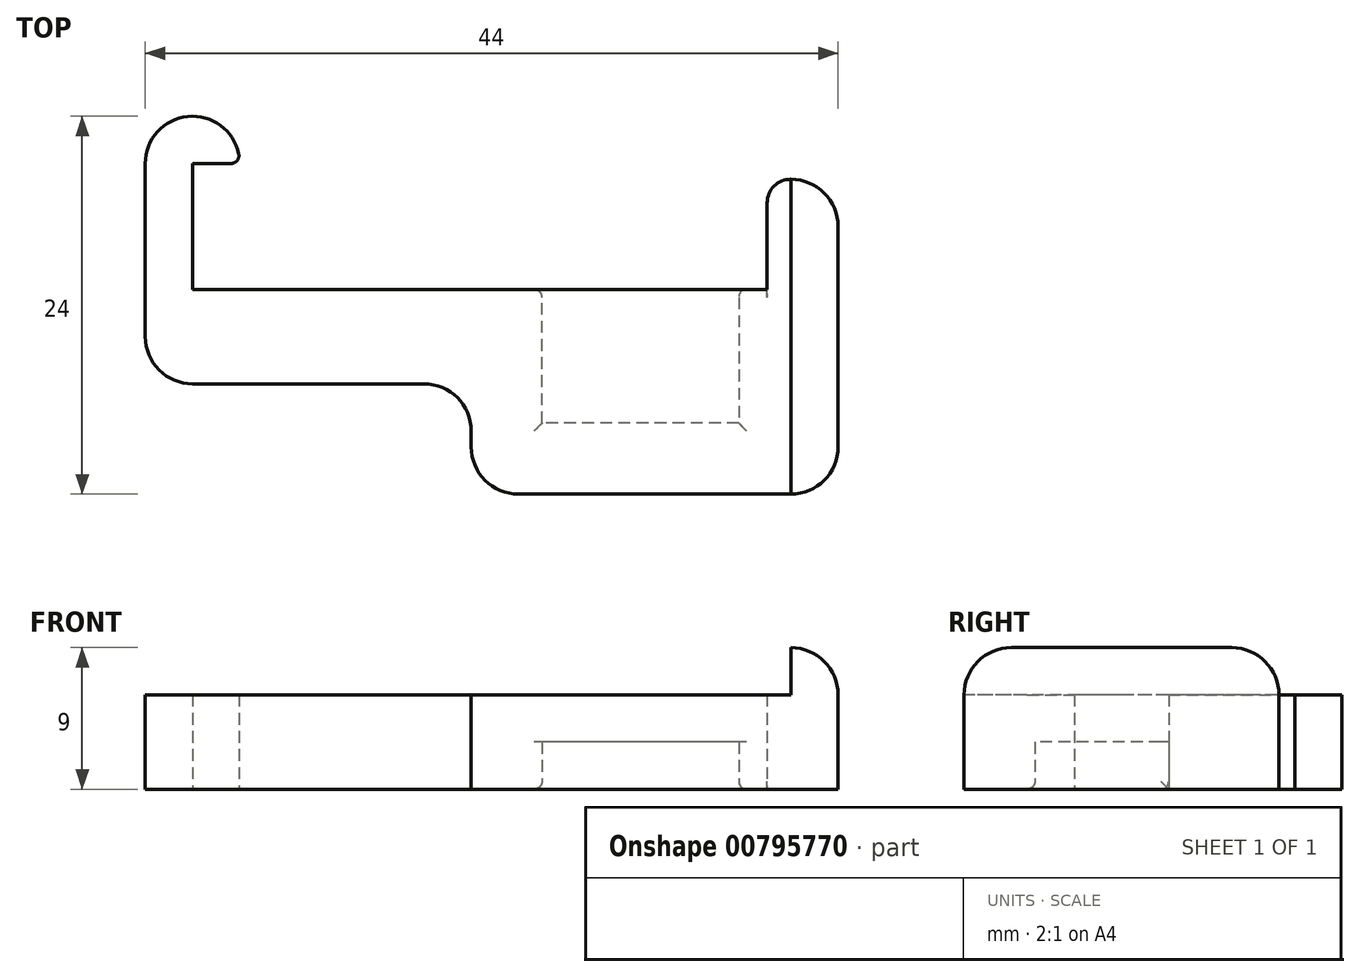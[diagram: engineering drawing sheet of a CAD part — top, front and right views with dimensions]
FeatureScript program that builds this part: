
annotation { "Feature Type Name" : "Feature", "Feature Type Description" : "" }
export const myFeature = defineFeature(function(context is Context, id is Id, definition is map)
    precondition{}
    {
        {
            var Q0;
            Q0=qCreatedBy(makeId("Top.planeOp"),FACE);
            var sketch = newSketch(context, id + "F0", { "sketchPlane" : qUnion([Q0])});
            skLineSegment(sketch, "E0", {"start": v(-39.5, -6) * mm, "end": v(-18.8, -6) * mm});
            skLineSegment(sketch, "E1", {"start": v(-18.8, -6) * mm, "end": v(-18.8, -13) * mm});
            skLineSegment(sketch, "E2", {"start": v(-18.8, -13) * mm, "end": v(4.5, -13) * mm});
            skLineSegment(sketch, "E3", {"start": v(4.5, -13) * mm, "end": v(4.5, 7) * mm});
            skLineSegment(sketch, "E4", {"start": v(4.5, 7) * mm, "end": v(0, 7) * mm});
            skLineSegment(sketch, "E5", {"start": v(0, 7) * mm, "end": v(0, 0) * mm});
            skLineSegment(sketch, "E6", {"start": v(0, 0) * mm, "end": v(-36.5, 0) * mm});
            skLineSegment(sketch, "E7", {"start": v(-36.5, 0) * mm, "end": v(-36.5, 8) * mm});
            skLineSegment(sketch, "E8", {"start": v(-36.5, 8) * mm, "end": v(-33.5, 8) * mm});
            skLineSegment(sketch, "E9", {"start": v(-33.5, 8) * mm, "end": v(-33.5, 11) * mm});
            skLineSegment(sketch, "E10", {"start": v(-33.5, 11) * mm, "end": v(-39.5, 11) * mm});
            skLineSegment(sketch, "E11", {"start": v(-39.5, 11) * mm, "end": v(-39.5, -6) * mm});
            skLineSegment(sketch, "E12", {"start": v(-1.8, 0) * mm, "end": v(-1.8, -8.5) * mm});
            skLineSegment(sketch, "E13", {"start": v(-1.8, -8.5) * mm, "end": v(-14.3, -8.5) * mm});
            skLineSegment(sketch, "E14", {"start": v(-14.3, -8.5) * mm, "end": v(-14.3, 0) * mm});
            skLineSegment(sketch, "E15", {"start": v(1.5, 7) * mm, "end": v(1.5, -13) * mm});
            skSolve(sketch);
        }
        {
            var Q0;
            Q0=makeQuery(id+"F0.imprint","IMPRINT",FACE,{"disambiguationData":[TD([[makeQuery(id+"F0.imprint","IMPRINT",EDGE,{"derivedFrom":sQuery(id+"F0.wireOp",EDGE,"E0")}),1.0]])]});
            extrude(context, id + "F1", {"entities" : qUnion([Q0]), "depth" : 1.5 * mm, "offsetDistance" : 25 * mm, "hasSecondDirection" : true, "secondDirectionOppositeDirection" : true, "secondDirectionDepth" : 4.5 * mm});
        }
        {
            var Q0;
            {var subQ0=sQuery(id+"F0.wireOp",EDGE,"E12");Q0=makeQuery(id+"F0.imprint","IMPRINT",FACE,{"disambiguationData":[TD([[makeQuery(id+"F0.imprint","IMPRINT",EDGE,{"derivedFrom":subQ0}),-1.0]])]});}
            extrude(context, id + "F2", {"entities" : qUnion([Q0]), "operationType" : NewBodyOperationType.ADD, "depth" : 1.5 * mm, "offsetDistance" : 25 * mm, "hasSecondDirection" : true, "secondDirectionOppositeDirection" : true, "secondDirectionDepth" : 1.5 * mm});
        }
        {
            var Q0;
            {var subQ0=sQuery(id+"F0.wireOp",EDGE,"E3");Q0=makeQuery(id+"F0.imprint","IMPRINT",FACE,{"disambiguationData":[TD([[makeQuery(id+"F0.imprint","IMPRINT",EDGE,{"derivedFrom":subQ0}),1.0]])]});}
            extrude(context, id + "F3", {"entities" : qUnion([Q0]), "operationType" : NewBodyOperationType.ADD, "depth" : 4.5 * mm, "offsetDistance" : 25 * mm, "hasSecondDirection" : true, "secondDirectionOppositeDirection" : true, "secondDirectionDepth" : 4.5 * mm});
        }
        {
            var Q0;
            Q0=makeQuery(id+"F1.opExtrude","SWEPT_EDGE",EDGE,{"disambiguationData":[OSD([sQuery(id+"F0.wireOp",EDGE,"E10"),sQuery(id+"F0.wireOp",EDGE,"E11")])]});
            var Q1;
            Q1=makeQuery(id+"F1.opExtrude","SWEPT_EDGE",EDGE,{"disambiguationData":[OSD([sQuery(id+"F0.wireOp",EDGE,"E9"),sQuery(id+"F0.wireOp",EDGE,"E10")])]});
            var Q2;
            Q2=makeQuery(id+"F1.opExtrude","SWEPT_EDGE",EDGE,{"disambiguationData":[OSD([sQuery(id+"F0.wireOp",EDGE,"E0"),sQuery(id+"F0.wireOp",EDGE,"E11")])]});
            var Q3;
            Q3=makeQuery(id+"F1.opExtrude","SWEPT_EDGE",EDGE,{"disambiguationData":[OSD([sQuery(id+"F0.wireOp",EDGE,"E0"),sQuery(id+"F0.wireOp",EDGE,"E1")])]});
            var Q4;
            Q4=makeQuery(id+"F1.opExtrude","SWEPT_EDGE",EDGE,{"disambiguationData":[OSD([sQuery(id+"F0.wireOp",EDGE,"E1"),sQuery(id+"F0.wireOp",EDGE,"E2")])]});
            var Q5;
            Q5=makeQuery(id+"F3.opExtrude","CAP_EDGE",EDGE,{"disambiguationData":[OSD([sQuery(id+"F0.wireOp",EDGE,"E4")])],"isStart":false});
            var Q6;
            Q6=makeQuery(id+"F3.opExtrude","SWEPT_EDGE",EDGE,{"disambiguationData":[OSD([sQuery(id+"F0.wireOp",EDGE,"E3"),sQuery(id+"F0.wireOp",EDGE,"E4")])]});
            var Q7;
            Q7=makeQuery(id+"F3.opExtrude","CAP_EDGE",EDGE,{"disambiguationData":[OSD([sQuery(id+"F0.wireOp",EDGE,"E3")])],"isStart":false});
            var Q8;
            Q8=makeQuery(id+"F3.opExtrude","CAP_EDGE",EDGE,{"disambiguationData":[OSD([sQuery(id+"F0.wireOp",EDGE,"E2")])],"isStart":false});
            var Q9;
            Q9=makeQuery(id+"F3.opExtrude","SWEPT_EDGE",EDGE,{"disambiguationData":[OSD([sQuery(id+"F0.wireOp",EDGE,"E2"),sQuery(id+"F0.wireOp",EDGE,"E3")])]});
            fillet(context, id + "F4", {"entities" : qUnion([Q0, Q1, Q2, Q3, Q4, Q5, Q6, Q7, Q8, Q9]), "radius" : 3 * mm, "tangentPropagation" : true, "allowEdgeOverflow" : false});
        }
        {
            var Q0;
            Q0=makeQuery(id+"F1.opExtrude","SWEPT_EDGE",EDGE,{"disambiguationData":[OSD([sQuery(id+"F0.wireOp",EDGE,"E4"),sQuery(id+"F0.wireOp",EDGE,"E5")])]});
            fillet(context, id + "F5", {"entities" : qUnion([Q0]), "radius" : 1.5 * mm, "tangentPropagation" : true, "allowEdgeOverflow" : false});
        }
        {
            var Q0;
            Q0=makeQuery(id+"F1.opExtrude","SWEPT_EDGE",EDGE,{"disambiguationData":[OSD([sQuery(id+"F0.wireOp",EDGE,"E6"),sQuery(id+"F0.wireOp",EDGE,"E12")])]});
            var Q1;
            Q1=makeQuery(id+"F1.opExtrude","CAP_EDGE",EDGE,{"disambiguationData":[OSD([sQuery(id+"F0.wireOp",EDGE,"E12")])],"isStart":true});
            var Q2;
            {var subQ0=sQuery(id+"F0.wireOp",EDGE,"E6");Q2=makeQuery(id+"F1.opExtrude","CAP_EDGE",EDGE,{"disambiguationData":[OSD([subQ0]),TDD([makeQuery(id+"F0.imprint","IMPRINT",EDGE,{"disambiguationData":[TD([[makeQuery(id+"F0.imprint","INTERSECT",VERTEX,{"derivedFrom":[sQuery(id+"F0.wireOp",EDGE,"E5"),subQ0]}),-1.0]])],"derivedFrom":subQ0})])],"isStart":true});}
            var Q3;
            Q3=makeQuery(id+"F1.opExtrude","CAP_EDGE",EDGE,{"disambiguationData":[OSD([sQuery(id+"F0.wireOp",EDGE,"E13")])],"isStart":true});
            var Q4;
            Q4=makeQuery(id+"F1.opExtrude","CAP_EDGE",EDGE,{"disambiguationData":[OSD([sQuery(id+"F0.wireOp",EDGE,"E14")])],"isStart":true});
            var Q5;
            Q5=makeQuery(id+"F1.opExtrude","SWEPT_EDGE",EDGE,{"disambiguationData":[OSD([sQuery(id+"F0.wireOp",EDGE,"E6"),sQuery(id+"F0.wireOp",EDGE,"E14")])]});
            var Q6;
            Q6=makeQuery(id+"F4.opFillet","BLEND_EDGE",EDGE,{"blendedFrom":[makeQuery(id+"F1.opExtrude","SWEPT_EDGE",EDGE,{"disambiguationData":[OSD([sQuery(id+"F0.wireOp",EDGE,"E9"),sQuery(id+"F0.wireOp",EDGE,"E10")])]}),makeQuery(id+"F1.opExtrude","SWEPT_FACE",FACE,{"disambiguationData":[OSD([sQuery(id+"F0.wireOp",EDGE,"E8")])]})],"blendedInto":[makeQuery(id+"F1.opExtrude","SWEPT_FACE",FACE,{"disambiguationData":[OSD([sQuery(id+"F0.wireOp",EDGE,"E8")])]})]});
            fillet(context, id + "F6", {"entities" : qUnion([Q0, Q1, Q2, Q3, Q4, Q5, Q6]), "radius" : 0.5 * mm, "tangentPropagation" : true, "allowEdgeOverflow" : false});
        }
    });
